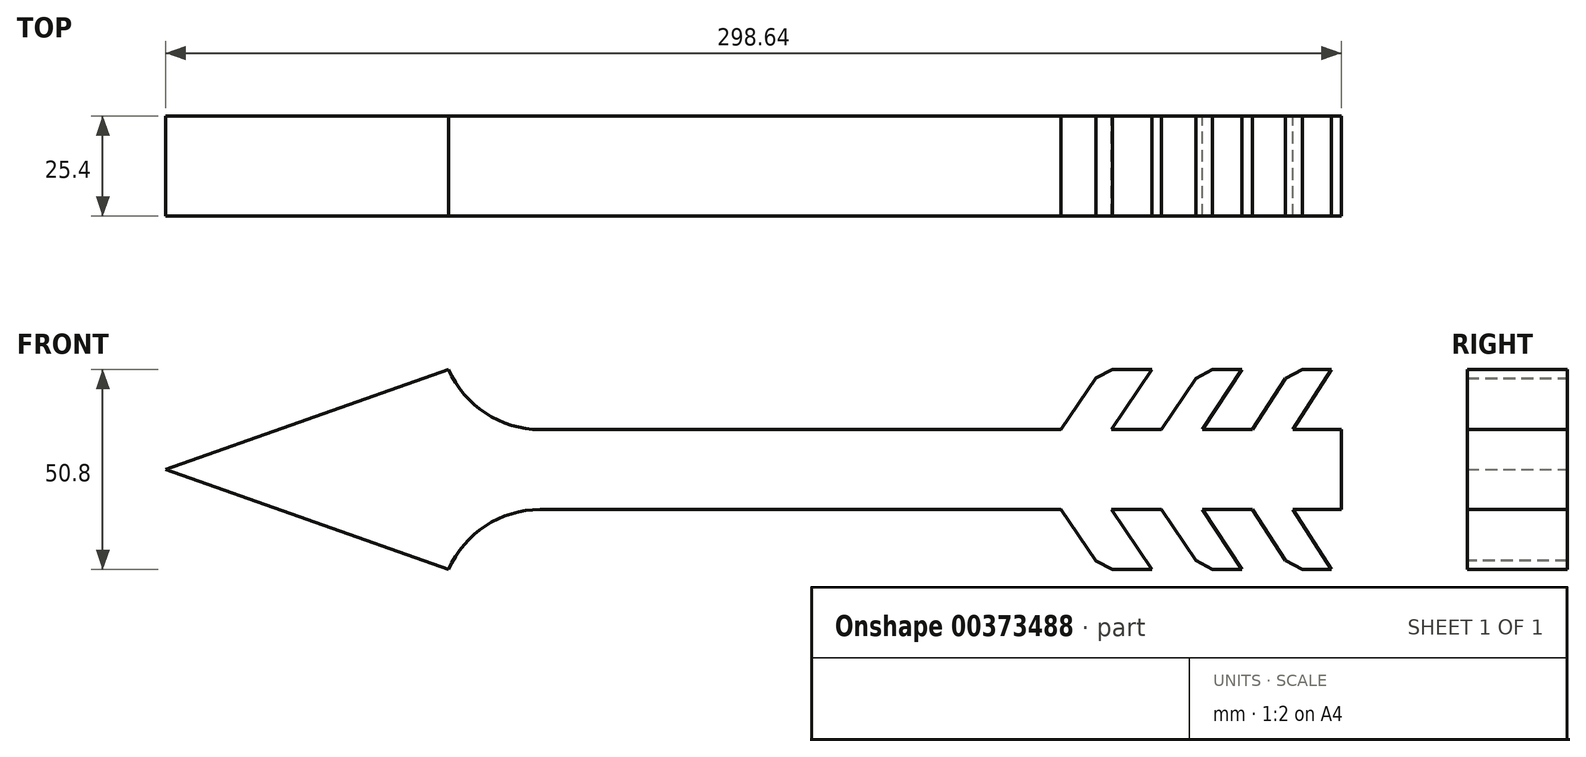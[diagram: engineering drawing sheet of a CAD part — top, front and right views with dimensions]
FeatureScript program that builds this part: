
annotation { "Feature Type Name" : "Feature", "Feature Type Description" : "" }
export const myFeature = defineFeature(function(context is Context, id is Id, definition is map)
    precondition{}
    {
        {
            var Q0;
            Q0=qCreatedBy(makeId("Front.planeOp"),FACE);
            var sketch = newSketch(context, id + "F0", { "sketchPlane" : qUnion([Q0])});
            skLineSegment(sketch, "E0", {"start": v(-234.6, 0.35) * mm, "end": v(-162.76, 25.75) * mm});
            skLineSegment(sketch, "E1", {"start": v(-162.76, 25.75) * mm, "end": v(-162.76, 10.5) * mm});
            skLineSegment(sketch, "E2", {"start": v(-162.76, 10.5) * mm, "end": v(-7.19, 10.5) * mm});
            skLineSegment(sketch, "E3", {"start": v(-7.19, 10.5) * mm, "end": v(3.25, 25.75) * mm});
            skLineSegment(sketch, "E4", {"start": v(3.25, 25.75) * mm, "end": v(15.95, 25.75) * mm});
            skLineSegment(sketch, "E5", {"start": v(15.95, 25.75) * mm, "end": v(5.67, 10.5) * mm});
            skLineSegment(sketch, "E6", {"start": v(5.67, 10.5) * mm, "end": v(18.37, 10.5) * mm});
            skLineSegment(sketch, "E7", {"start": v(18.37, 10.5) * mm, "end": v(28.6, 25.75) * mm});
            skLineSegment(sketch, "E8", {"start": v(28.6, 25.75) * mm, "end": v(38.76, 25.75) * mm});
            skLineSegment(sketch, "E9", {"start": v(38.76, 25.75) * mm, "end": v(28.72, 10.5) * mm});
            skLineSegment(sketch, "E10", {"start": v(28.72, 10.5) * mm, "end": v(41.42, 10.5) * mm});
            skLineSegment(sketch, "E11", {"start": v(41.42, 10.5) * mm, "end": v(51.4, 25.75) * mm});
            skLineSegment(sketch, "E12", {"start": v(51.4, 25.75) * mm, "end": v(61.56, 25.75) * mm});
            skLineSegment(sketch, "E13", {"start": v(61.56, 25.75) * mm, "end": v(51.77, 10.5) * mm});
            skLineSegment(sketch, "E14", {"start": v(51.77, 10.5) * mm, "end": v(64.04, 10.5) * mm});
            skLineSegment(sketch, "E15", {"start": v(64.04, 10.5) * mm, "end": v(64.04, 0.35) * mm});
            skLineSegment(sketch, "E16", {"start": v(-234.6, 0.35) * mm, "end": v(64.04, 0.35) * mm});
            skLineSegment(sketch, "E17.MirrorCS", {"start": v(-162.76, -9.81) * mm, "end": v(-7.19, -9.81) * mm});
            skLineSegment(sketch, "E18.MirrorCS", {"start": v(-162.76, -25.05) * mm, "end": v(-162.76, -9.81) * mm});
            skLineSegment(sketch, "E19.MirrorCS", {"start": v(-234.6, 0.35) * mm, "end": v(-162.76, -25.05) * mm});
            skLineSegment(sketch, "E20.MirrorCS", {"start": v(-7.19, -9.81) * mm, "end": v(3.25, -25.05) * mm});
            skLineSegment(sketch, "E21.MirrorCS", {"start": v(15.95, -25.05) * mm, "end": v(5.67, -9.81) * mm});
            skLineSegment(sketch, "E22.MirrorCS", {"start": v(18.37, -9.81) * mm, "end": v(28.6, -25.05) * mm});
            skLineSegment(sketch, "E23.MirrorCS", {"start": v(38.76, -25.05) * mm, "end": v(28.72, -9.81) * mm});
            skLineSegment(sketch, "E24.MirrorCS", {"start": v(41.42, -9.81) * mm, "end": v(51.4, -25.05) * mm});
            skLineSegment(sketch, "E25.MirrorCS", {"start": v(61.56, -25.05) * mm, "end": v(51.77, -9.81) * mm});
            skLineSegment(sketch, "E26.MirrorCS", {"start": v(64.04, -9.81) * mm, "end": v(64.04, 0.35) * mm});
            skLineSegment(sketch, "E27.MirrorCS", {"start": v(51.77, -9.81) * mm, "end": v(64.04, -9.81) * mm});
            skLineSegment(sketch, "E28.MirrorCS", {"start": v(5.67, -9.81) * mm, "end": v(18.37, -9.81) * mm});
            skLineSegment(sketch, "E29.MirrorCS", {"start": v(28.72, -9.81) * mm, "end": v(41.42, -9.81) * mm});
            skLineSegment(sketch, "E30", {"start": v(-7.19, 10.5) * mm, "end": v(5.67, 10.5) * mm});
            skLineSegment(sketch, "E31", {"start": v(41.42, 10.5) * mm, "end": v(51.77, 10.5) * mm});
            skLineSegment(sketch, "E32", {"start": v(18.37, 10.5) * mm, "end": v(28.72, 10.5) * mm});
            skLineSegment(sketch, "E33.MirrorCS", {"start": v(-7.19, -9.81) * mm, "end": v(5.67, -9.81) * mm});
            skLineSegment(sketch, "E34.MirrorCS", {"start": v(18.37, -9.81) * mm, "end": v(28.72, -9.81) * mm});
            skLineSegment(sketch, "E35.MirrorCS", {"start": v(41.42, -9.81) * mm, "end": v(51.77, -9.81) * mm});
            skLineSegment(sketch, "E36", {"start": v(3.25, -25.05) * mm, "end": v(15.95, -25.05) * mm});
            skLineSegment(sketch, "E37", {"start": v(28.6, -25.05) * mm, "end": v(38.76, -25.05) * mm});
            skLineSegment(sketch, "E38", {"start": v(51.4, -25.05) * mm, "end": v(61.56, -25.05) * mm});
            skSolve(sketch);
        }
        {
            var Q0;
            Q0 = qSketchRegion(id + "F0", true);
            extrude(context, id + "F1", {"entities" : qUnion([Q0]), "depth" : 25.4 * mm});
        }
        {
            var Q0;
            Q0=makeQuery(id+"F1.opExtrude","SWEPT_EDGE",EDGE,{"disambiguationData":[OSD([sQuery(id+"F0.wireOp",EDGE,"E1"),sQuery(id+"F0.wireOp",EDGE,"E2")])]});
            var Q1;
            Q1=makeQuery(id+"F1.opExtrude","SWEPT_EDGE",EDGE,{"disambiguationData":[OSD([sQuery(id+"F0.wireOp",EDGE,"E18.MirrorCS"),sQuery(id+"F0.wireOp",EDGE,"E17.MirrorCS")])]});
            fillet(context, id + "F2", {"entities" : qUnion([Q0, Q1]), "radius" : 25.4 * mm, "tangentPropagation" : true, "allowEdgeOverflow" : false});
        }
        {
            var Q0;
            Q0=makeQuery(id+"F1.opExtrude","SWEPT_EDGE",EDGE,{"disambiguationData":[OSD([sQuery(id+"F0.wireOp",EDGE,"E3"),sQuery(id+"F0.wireOp",EDGE,"E4")])]});
            var Q1;
            Q1=makeQuery(id+"F1.opExtrude","SWEPT_EDGE",EDGE,{"disambiguationData":[OSD([sQuery(id+"F0.wireOp",EDGE,"E7"),sQuery(id+"F0.wireOp",EDGE,"E8")])]});
            var Q2;
            Q2=makeQuery(id+"F1.opExtrude","SWEPT_EDGE",EDGE,{"disambiguationData":[OSD([sQuery(id+"F0.wireOp",EDGE,"E11"),sQuery(id+"F0.wireOp",EDGE,"E12")])]});
            var Q3;
            Q3=makeQuery(id+"F1.opExtrude","SWEPT_EDGE",EDGE,{"disambiguationData":[OSD([sQuery(id+"F0.wireOp",EDGE,"E24.MirrorCS"),sQuery(id+"F0.wireOp",EDGE,"E38")])]});
            var Q4;
            Q4=makeQuery(id+"F1.opExtrude","SWEPT_EDGE",EDGE,{"disambiguationData":[OSD([sQuery(id+"F0.wireOp",EDGE,"E20.MirrorCS"),sQuery(id+"F0.wireOp",EDGE,"E36")])]});
            var Q5;
            Q5=makeQuery(id+"F1.opExtrude","SWEPT_EDGE",EDGE,{"disambiguationData":[OSD([sQuery(id+"F0.wireOp",EDGE,"E22.MirrorCS"),sQuery(id+"F0.wireOp",EDGE,"E37")])]});
            chamfer(context, id + "F3", {"entities" : qUnion([Q0, Q1, Q2, Q3, Q4, Q5]), "width" : 5.08 * mm, "tangentPropagation" : true});
        }
    });
